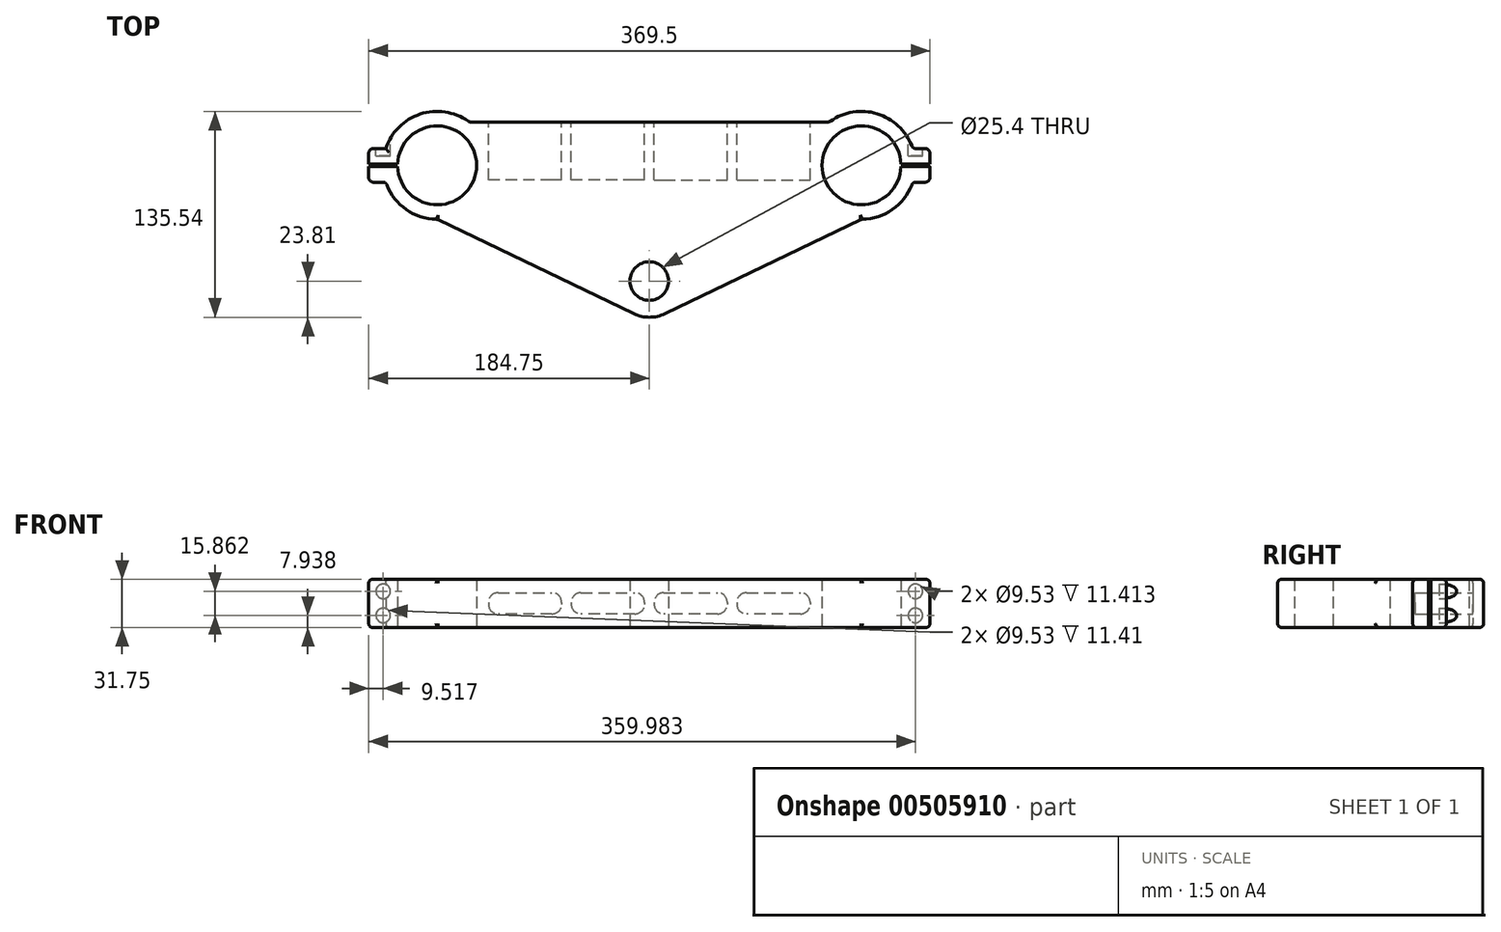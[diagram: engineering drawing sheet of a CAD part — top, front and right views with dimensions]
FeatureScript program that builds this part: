
annotation { "Feature Type Name" : "Feature", "Feature Type Description" : "" }
export const myFeature = defineFeature(function(context is Context, id is Id, definition is map)
    precondition{}
    {
        {
            var Q0;
            Q0=qCreatedBy(makeId("Top.planeOp"),FACE);
            var sketch = newSketch(context, id + "F0", { "sketchPlane" : qUnion([Q0])});
            skArc(sketch, "E0", {"start": v(165.69, 0.8) * mm, "mid": v(113.7, 0) * mm, "end": v(165.69, -0.8) * mm});
            skCircle(sketch, "E1", {"center": v(0, -76.2) * mm, "radius": 12.7 * mm});
            skArc(sketch, "E2.0", {"start": v(139.7, -35.52) * mm, "mid": v(160.52, -28.78) * mm, "end": v(173.44, -11.11) * mm});
            skArc(sketch, "E3.0", {"start": v(-10.3, -97.67) * mm, "mid": v(0, -100.01) * mm, "end": v(10.3, -97.67) * mm});
            skLineSegment(sketch, "E4", {"start": v(139.7, -35.52) * mm, "end": v(10.3, -97.67) * mm});
            skArc(sketch, "E5.MirrorC", {"start": v(-139.7, -35.52) * mm, "mid": v(-160.52, -28.78) * mm, "end": v(-173.44, -11.11) * mm});
            skArc(sketch, "E6.MirrorC", {"start": v(-165.69, 0.8) * mm, "mid": v(-113.7, 0) * mm, "end": v(-165.69, -0.8) * mm});
            skLineSegment(sketch, "E7.MirrorCS", {"start": v(-139.7, -35.52) * mm, "end": v(-10.3, -97.67) * mm});
            skLineSegment(sketch, "E8", {"start": v(0, 28.58) * mm, "end": v(118.6, 28.58) * mm});
            skLineSegment(sketch, "E9.MirrorCS", {"start": v(0, 28.58) * mm, "end": v(-118.6, 28.57) * mm});
            skLineSegment(sketch, "E10", {"start": v(-173.44, 11.11) * mm, "end": v(-181.58, 11.11) * mm});
            skLineSegment(sketch, "E11", {"start": v(-184.75, 7.94) * mm, "end": v(-184.75, 0.8) * mm});
            skLineSegment(sketch, "E12", {"start": v(-181.58, -11.11) * mm, "end": v(-173.44, -11.11) * mm});
            skPoint(sketch, "E13", {"position": v(-184.75, 0) * mm});
            skLineSegment(sketch, "E14", {"start": v(139.7, 0) * mm, "end": v(-207.33, 0) * mm, "construction": true});
            skArc(sketch, "E15.trimOffspring", {"start": v(-173.44, 11.11) * mm, "mid": v(-150.48, 33.85) * mm, "end": v(-118.6, 28.58) * mm});
            skPoint(sketch, "E16.visualSharp", {"position": v(-184.75, 11.11) * mm});
            skArc(sketch, "E16.filletArc", {"start": v(-181.58, 11.11) * mm, "mid": v(-183.82, 10.18) * mm, "end": v(-184.75, 7.94) * mm});
            skPoint(sketch, "E17.visualSharp", {"position": v(-184.75, -11.11) * mm});
            skArc(sketch, "E17.filletArc", {"start": v(-184.75, -7.94) * mm, "mid": v(-183.82, -10.18) * mm, "end": v(-181.58, -11.11) * mm});
            skLineSegment(sketch, "E18.MirrorCS", {"start": v(173.44, 11.11) * mm, "end": v(181.58, 11.11) * mm});
            skArc(sketch, "E19.MirrorCS", {"start": v(181.58, 11.11) * mm, "mid": v(183.82, 10.18) * mm, "end": v(184.75, 7.94) * mm});
            skLineSegment(sketch, "E20.MirrorCS", {"start": v(184.75, 7.94) * mm, "end": v(184.75, 0.8) * mm});
            skArc(sketch, "E21.MirrorCS", {"start": v(184.75, -7.94) * mm, "mid": v(183.82, -10.18) * mm, "end": v(181.58, -11.11) * mm});
            skLineSegment(sketch, "E22.MirrorCS", {"start": v(181.58, -11.11) * mm, "end": v(173.44, -11.11) * mm});
            skArc(sketch, "E23.trimOffspring", {"start": v(173.44, 11.11) * mm, "mid": v(150.48, 33.85) * mm, "end": v(118.6, 28.58) * mm});
            skLineSegment(sketch, "E24", {"start": v(-184.75, 0.8) * mm, "end": v(-165.69, 0.8) * mm});
            skLineSegment(sketch, "E25.MirrorCS", {"start": v(-184.75, -0.8) * mm, "end": v(-165.69, -0.8) * mm});
            skLineSegment(sketch, "E26.trimOffspring", {"start": v(-184.75, -0.8) * mm, "end": v(-184.75, -7.94) * mm});
            skLineSegment(sketch, "E27.MirrorCS", {"start": v(184.75, 0.8) * mm, "end": v(165.69, 0.8) * mm});
            skLineSegment(sketch, "E28.MirrorCS", {"start": v(184.75, -0.8) * mm, "end": v(165.69, -0.8) * mm});
            skLineSegment(sketch, "E29.trimOffspring", {"start": v(184.75, -0.8) * mm, "end": v(184.75, -7.94) * mm});
            skSolve(sketch);
        }
        {
            var Q0;
            Q0 = qSketchRegion(id + "F0", true);
            extrude(context, id + "F1", {"entities" : qUnion([Q0]), "depth" : 31.75 * mm});
        }
        {
            var Q0;
            Q0=makeQuery(id+"F1.opExtrude","CAP_EDGE",EDGE,{"disambiguationData":[OSD([sQuery(id+"F0.wireOp",EDGE,"E2.0")])],"isStart":false});
            var Q1;
            Q1=makeQuery(id+"F1.opExtrude","CAP_EDGE",EDGE,{"disambiguationData":[OSD([sQuery(id+"F0.wireOp",EDGE,"E8"),sQuery(id+"F0.wireOp",EDGE,"E9.MirrorCS")])],"isStart":false});
            var Q2;
            Q2=makeQuery(id+"F1.opExtrude","CAP_EDGE",EDGE,{"disambiguationData":[OSD([sQuery(id+"F0.wireOp",EDGE,"E5.MirrorC")])],"isStart":false});
            var Q3;
            Q3=makeQuery(id+"F1.opExtrude","CAP_EDGE",EDGE,{"disambiguationData":[OSD([sQuery(id+"F0.wireOp",EDGE,"E7.MirrorCS")])],"isStart":false});
            var Q4;
            Q4=makeQuery(id+"F1.opExtrude","CAP_EDGE",EDGE,{"disambiguationData":[OSD([sQuery(id+"F0.wireOp",EDGE,"E3.0")])],"isStart":false});
            var Q5;
            Q5=makeQuery(id+"F1.opExtrude","CAP_EDGE",EDGE,{"disambiguationData":[OSD([sQuery(id+"F0.wireOp",EDGE,"E4")])],"isStart":false});
            var Q6;
            Q6=makeQuery(id+"F1.opExtrude","CAP_EDGE",EDGE,{"disambiguationData":[OSD([sQuery(id+"F0.wireOp",EDGE,"E7.MirrorCS")])],"isStart":true});
            var Q7;
            Q7=makeQuery(id+"F1.opExtrude","CAP_EDGE",EDGE,{"disambiguationData":[OSD([sQuery(id+"F0.wireOp",EDGE,"E5.MirrorC")])],"isStart":true});
            var Q8;
            Q8=makeQuery(id+"F1.opExtrude","CAP_EDGE",EDGE,{"disambiguationData":[OSD([sQuery(id+"F0.wireOp",EDGE,"E8"),sQuery(id+"F0.wireOp",EDGE,"E9.MirrorCS")])],"isStart":true});
            var Q9;
            Q9=makeQuery(id+"F1.opExtrude","CAP_EDGE",EDGE,{"disambiguationData":[OSD([sQuery(id+"F0.wireOp",EDGE,"E2.0")])],"isStart":true});
            var Q10;
            Q10=makeQuery(id+"F1.opExtrude","CAP_EDGE",EDGE,{"disambiguationData":[OSD([sQuery(id+"F0.wireOp",EDGE,"E4")])],"isStart":true});
            var Q11;
            Q11=makeQuery(id+"F1.opExtrude","CAP_EDGE",EDGE,{"disambiguationData":[OSD([sQuery(id+"F0.wireOp",EDGE,"E3.0")])],"isStart":true});
            var Q12;
            Q12=makeQuery(id+"F1.opExtrude","CAP_EDGE",EDGE,{"disambiguationData":[OSD([sQuery(id+"F0.wireOp",EDGE,"E23.trimOffspring")])],"isStart":true});
            var Q13;
            Q13=makeQuery(id+"F1.opExtrude","CAP_EDGE",EDGE,{"disambiguationData":[OSD([sQuery(id+"F0.wireOp",EDGE,"E19.MirrorCS")])],"isStart":true});
            var Q14;
            Q14=makeQuery(id+"F1.opExtrude","CAP_EDGE",EDGE,{"disambiguationData":[OSD([sQuery(id+"F0.wireOp",EDGE,"E21.MirrorCS")])],"isStart":true});
            var Q15;
            Q15=makeQuery(id+"F1.opExtrude","CAP_EDGE",EDGE,{"disambiguationData":[OSD([sQuery(id+"F0.wireOp",EDGE,"E23.trimOffspring")])],"isStart":false});
            var Q16;
            Q16=makeQuery(id+"F1.opExtrude","CAP_EDGE",EDGE,{"disambiguationData":[OSD([sQuery(id+"F0.wireOp",EDGE,"E19.MirrorCS")])],"isStart":false});
            var Q17;
            Q17=makeQuery(id+"F1.opExtrude","CAP_EDGE",EDGE,{"disambiguationData":[OSD([sQuery(id+"F0.wireOp",EDGE,"E21.MirrorCS")])],"isStart":false});
            var Q18;
            Q18=makeQuery(id+"F1.opExtrude","SWEPT_EDGE",EDGE,{"disambiguationData":[OSD([sQuery(id+"F0.wireOp",EDGE,"E2.0"),sQuery(id+"F0.wireOp",EDGE,"E22.MirrorCS")])]});
            var Q19;
            Q19=makeQuery(id+"F1.opExtrude","SWEPT_EDGE",EDGE,{"disambiguationData":[OSD([sQuery(id+"F0.wireOp",EDGE,"E18.MirrorCS"),sQuery(id+"F0.wireOp",EDGE,"E23.trimOffspring")])]});
            var Q20;
            Q20=makeQuery(id+"F1.opExtrude","SWEPT_EDGE",EDGE,{"disambiguationData":[OSD([sQuery(id+"F0.wireOp",EDGE,"E8"),sQuery(id+"F0.wireOp",EDGE,"E23.trimOffspring")])]});
            fillet(context, id + "F2", {"entities" : qUnion([Q0, Q1, Q2, Q3, Q4, Q5, Q6, Q7, Q8, Q9, Q10, Q11, Q12, Q13, Q14, Q15, Q16, Q17, Q18, Q19, Q20]), "radius" : 2.54 * mm, "tangentPropagation" : true, "allowEdgeOverflow" : false});
        }
        {
            var Q0;
            Q0=makeQuery(id+"F1.opExtrude","SWEPT_FACE",FACE,{"disambiguationData":[OSD([sQuery(id+"F0.wireOp",EDGE,"E8"),sQuery(id+"F0.wireOp",EDGE,"E9.MirrorCS")])]});
            var sketch = newSketch(context, id + "F3", { "sketchPlane" : qUnion([Q0])});
            skLineSegment(sketch, "E30.0", {"start": v(99.54, 22.86) * mm, "end": v(64.06, 22.86) * mm});
            skLineSegment(sketch, "E31.0", {"start": v(-99.54, 8.9) * mm, "end": v(-64.06, 8.9) * mm});
            skLineSegment(sketch, "E32.0", {"start": v(-105.9, 16.5) * mm, "end": v(-105.9, 15.24) * mm});
            skLineSegment(sketch, "E33.0", {"start": v(105.9, 16.5) * mm, "end": v(105.9, 15.24) * mm});
            skLineSegment(sketch, "E34", {"start": v(-57.7, 16.51) * mm, "end": v(-57.7, 15.24) * mm});
            skLineSegment(sketch, "E35", {"start": v(-51.36, 16.51) * mm, "end": v(-51.36, 15.24) * mm});
            skLineSegment(sketch, "E36", {"start": v(-3.18, 16.5) * mm, "end": v(-3.18, 15.24) * mm});
            skLineSegment(sketch, "E37", {"start": v(3.17, 16.5) * mm, "end": v(3.17, 15.24) * mm});
            skLineSegment(sketch, "E38", {"start": v(57.7, 16.51) * mm, "end": v(57.7, 15.24) * mm});
            skLineSegment(sketch, "E39", {"start": v(51.36, 16.51) * mm, "end": v(51.36, 15.24) * mm});
            skLineSegment(sketch, "E40.trimOffspring", {"start": v(-45, 8.9) * mm, "end": v(-9.53, 8.9) * mm});
            skLineSegment(sketch, "E41.trimOffspring", {"start": v(-64.06, 22.86) * mm, "end": v(-99.54, 22.86) * mm});
            skLineSegment(sketch, "E42.trimOffspring", {"start": v(9.52, 8.9) * mm, "end": v(45, 8.9) * mm});
            skLineSegment(sketch, "E43.trimOffspring", {"start": v(-9.53, 22.86) * mm, "end": v(-45, 22.86) * mm});
            skLineSegment(sketch, "E44.trimOffspring", {"start": v(64.06, 8.9) * mm, "end": v(99.54, 8.9) * mm});
            skLineSegment(sketch, "E45.trimOffspring", {"start": v(45, 22.86) * mm, "end": v(9.52, 22.86) * mm});
            skPoint(sketch, "E46.visualSharp", {"position": v(-105.9, 22.86) * mm});
            skArc(sketch, "E46.filletArc", {"start": v(-99.54, 22.86) * mm, "mid": v(-104.03, 21) * mm, "end": v(-105.9, 16.5) * mm});
            skPoint(sketch, "E47.visualSharp", {"position": v(-57.7, 22.86) * mm});
            skArc(sketch, "E47.filletArc", {"start": v(-57.7, 16.51) * mm, "mid": v(-59.57, 21) * mm, "end": v(-64.06, 22.86) * mm});
            skPoint(sketch, "E48.visualSharp", {"position": v(-57.7, 8.9) * mm});
            skArc(sketch, "E48.filletArc", {"start": v(-64.06, 8.89) * mm, "mid": v(-59.57, 10.75) * mm, "end": v(-57.7, 15.24) * mm});
            skPoint(sketch, "E49.visualSharp", {"position": v(-105.9, 8.9) * mm});
            skArc(sketch, "E49.filletArc", {"start": v(-105.9, 15.24) * mm, "mid": v(-104.03, 10.75) * mm, "end": v(-99.54, 8.89) * mm});
            skPoint(sketch, "E50.visualSharp", {"position": v(-51.36, 22.86) * mm});
            skArc(sketch, "E50.filletArc", {"start": v(-45, 22.86) * mm, "mid": v(-49.5, 21) * mm, "end": v(-51.36, 16.51) * mm});
            skPoint(sketch, "E51.visualSharp", {"position": v(-3.18, 8.9) * mm});
            skArc(sketch, "E51.filletArc", {"start": v(-9.53, 8.9) * mm, "mid": v(-5.03, 10.75) * mm, "end": v(-3.18, 15.24) * mm});
            skPoint(sketch, "E52.visualSharp", {"position": v(-3.18, 22.86) * mm});
            skArc(sketch, "E52.filletArc", {"start": v(-3.18, 16.5) * mm, "mid": v(-5.03, 21) * mm, "end": v(-9.53, 22.86) * mm});
            skPoint(sketch, "E53.visualSharp", {"position": v(-51.36, 8.9) * mm});
            skArc(sketch, "E53.filletArc", {"start": v(-51.36, 15.24) * mm, "mid": v(-49.5, 10.75) * mm, "end": v(-45, 8.89) * mm});
            skPoint(sketch, "E54.visualSharp", {"position": v(3.17, 22.86) * mm});
            skArc(sketch, "E54.filletArc", {"start": v(9.52, 22.86) * mm, "mid": v(5.03, 21) * mm, "end": v(3.17, 16.5) * mm});
            skPoint(sketch, "E55.visualSharp", {"position": v(3.17, 8.9) * mm});
            skArc(sketch, "E55.filletArc", {"start": v(3.17, 15.24) * mm, "mid": v(5.03, 10.75) * mm, "end": v(9.52, 8.9) * mm});
            skPoint(sketch, "E56.visualSharp", {"position": v(51.36, 8.9) * mm});
            skArc(sketch, "E56.filletArc", {"start": v(45, 8.89) * mm, "mid": v(49.5, 10.75) * mm, "end": v(51.36, 15.24) * mm});
            skPoint(sketch, "E57.visualSharp", {"position": v(51.36, 22.86) * mm});
            skArc(sketch, "E57.filletArc", {"start": v(51.36, 16.51) * mm, "mid": v(49.5, 21) * mm, "end": v(45, 22.86) * mm});
            skPoint(sketch, "E58.visualSharp", {"position": v(57.7, 22.86) * mm});
            skArc(sketch, "E58.filletArc", {"start": v(64.06, 22.86) * mm, "mid": v(59.57, 21) * mm, "end": v(57.7, 16.51) * mm});
            skPoint(sketch, "E59.visualSharp", {"position": v(57.7, 8.9) * mm});
            skArc(sketch, "E59.filletArc", {"start": v(57.7, 15.24) * mm, "mid": v(59.57, 10.75) * mm, "end": v(64.06, 8.89) * mm});
            skPoint(sketch, "E60.visualSharp", {"position": v(105.9, 8.9) * mm});
            skArc(sketch, "E60.filletArc", {"start": v(99.54, 8.89) * mm, "mid": v(104.03, 10.75) * mm, "end": v(105.9, 15.24) * mm});
            skPoint(sketch, "E61.visualSharp", {"position": v(105.9, 22.86) * mm});
            skArc(sketch, "E61.filletArc", {"start": v(105.9, 16.5) * mm, "mid": v(104.03, 21) * mm, "end": v(99.54, 22.86) * mm});
            skSolve(sketch);
        }
        {
            var Q0;
            Q0 = qSketchRegion(id + "F3", true);
            extrude(context, id + "F4", {"entities" : qUnion([Q0]), "operationType" : NewBodyOperationType.REMOVE, "oppositeDirection" : true, "depth" : 38.1 * mm});
        }
        {
            var Q0;
            Q0=makeQuery(id+"F4.boolean.opBoolean","COPY",EDGE,{"derivedFrom":makeQuery(id+"F4.opExtrude","CAP_EDGE",EDGE,{"disambiguationData":[OSD([sQuery(id+"F3.wireOp",EDGE,"E41.trimOffspring")])],"isStart":true})});
            var Q1;
            Q1=makeQuery(id+"F4.boolean.opBoolean","COPY",EDGE,{"derivedFrom":makeQuery(id+"F4.opExtrude","CAP_EDGE",EDGE,{"disambiguationData":[OSD([sQuery(id+"F3.wireOp",EDGE,"E43.trimOffspring")])],"isStart":true})});
            var Q2;
            Q2=makeQuery(id+"F4.boolean.opBoolean","COPY",EDGE,{"derivedFrom":makeQuery(id+"F4.opExtrude","CAP_EDGE",EDGE,{"disambiguationData":[OSD([sQuery(id+"F3.wireOp",EDGE,"E45.trimOffspring")])],"isStart":true})});
            var Q3;
            Q3=makeQuery(id+"F4.boolean.opBoolean","COPY",EDGE,{"derivedFrom":makeQuery(id+"F4.opExtrude","CAP_EDGE",EDGE,{"disambiguationData":[OSD([sQuery(id+"F3.wireOp",EDGE,"E30.0")])],"isStart":true})});
            var Q4;
            Q4=makeQuery(id+"F1.opExtrude","SWEPT_EDGE",EDGE,{"disambiguationData":[OSD([sQuery(id+"F0.wireOp",EDGE,"E2.0"),sQuery(id+"F0.wireOp",EDGE,"E8")])]});
            var Q5;
            Q5=makeQuery(id+"F1.opExtrude","SWEPT_EDGE",EDGE,{"disambiguationData":[OSD([sQuery(id+"F0.wireOp",EDGE,"E5.MirrorC"),sQuery(id+"F0.wireOp",EDGE,"E9.MirrorCS")])]});
            fillet(context, id + "F5", {"entities" : qUnion([Q0, Q1, Q2, Q3, Q4, Q5]), "radius" : 2.54 * mm, "tangentPropagation" : true, "allowEdgeOverflow" : false});
        }
        {
            var Q0;
            Q0=makeQuery(id+"F1.opExtrude","SWEPT_EDGE",EDGE,{"disambiguationData":[OSD([sQuery(id+"F0.wireOp",EDGE,"E18.MirrorCS"),sQuery(id+"F0.wireOp",EDGE,"E23.trimOffspring")])]});
            var Q1;
            Q1=makeQuery(id+"F1.opExtrude","CAP_EDGE",EDGE,{"disambiguationData":[OSD([sQuery(id+"F0.wireOp",EDGE,"E22.MirrorCS")])],"isStart":false});
            var Q2;
            Q2=makeQuery(id+"F1.opExtrude","CAP_EDGE",EDGE,{"disambiguationData":[OSD([sQuery(id+"F0.wireOp",EDGE,"E20.MirrorCS")])],"isStart":false});
            var Q3;
            Q3=makeQuery(id+"F1.opExtrude","CAP_EDGE",EDGE,{"disambiguationData":[OSD([sQuery(id+"F0.wireOp",EDGE,"E15.trimOffspring")])],"isStart":false});
            var Q4;
            Q4=makeQuery(id+"F1.opExtrude","CAP_EDGE",EDGE,{"disambiguationData":[OSD([sQuery(id+"F0.wireOp",EDGE,"E10")])],"isStart":false});
            var Q5;
            Q5=makeQuery(id+"F1.opExtrude","CAP_EDGE",EDGE,{"disambiguationData":[OSD([sQuery(id+"F0.wireOp",EDGE,"E26.trimOffspring")])],"isStart":false});
            var Q6;
            Q6=makeQuery(id+"F1.opExtrude","CAP_EDGE",EDGE,{"disambiguationData":[OSD([sQuery(id+"F0.wireOp",EDGE,"E15.trimOffspring")])],"isStart":true});
            var Q7;
            Q7=makeQuery(id+"F1.opExtrude","CAP_EDGE",EDGE,{"disambiguationData":[OSD([sQuery(id+"F0.wireOp",EDGE,"E16.filletArc")])],"isStart":true});
            var Q8;
            Q8=makeQuery(id+"F1.opExtrude","CAP_EDGE",EDGE,{"disambiguationData":[OSD([sQuery(id+"F0.wireOp",EDGE,"E17.filletArc")])],"isStart":true});
            fillet(context, id + "F6", {"entities" : qUnion([Q0, Q1, Q2, Q3, Q4, Q5, Q6, Q7, Q8]), "radius" : 2.54 * mm, "tangentPropagation" : true, "allowEdgeOverflow" : false});
        }
        {
            var Q0;
            Q0=makeQuery(id+"F1.opExtrude","SWEPT_FACE",FACE,{"disambiguationData":[OSD([sQuery(id+"F0.wireOp",EDGE,"E18.MirrorCS")])]});
            var sketch = newSketch(context, id + "F7", { "sketchPlane" : qUnion([Q0])});
            skCircle(sketch, "E62", {"center": v(-175.23, 23.8) * mm, "radius": 4.76 * mm});
            skCircle(sketch, "E63", {"center": v(-175.23, 7.94) * mm, "radius": 4.76 * mm});
            skCircle(sketch, "E64.MirrorC", {"center": v(175.23, 23.8) * mm, "radius": 4.76 * mm});
            skCircle(sketch, "E65.MirrorC", {"center": v(175.23, 7.94) * mm, "radius": 4.76 * mm});
            skSolve(sketch);
        }
        {
            var Q0;
            Q0 = qSketchRegion(id + "F7", true);
            extrude(context, id + "F8", {"entities" : qUnion([Q0]), "operationType" : NewBodyOperationType.REMOVE, "oppositeDirection" : true, "depth" : 4.76 * mm, "hasSecondDirection" : true, "secondDirectionOppositeDirection" : false, "secondDirectionDepth" : 25.4 * mm});
        }
    });
